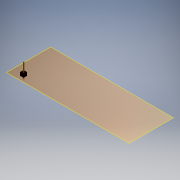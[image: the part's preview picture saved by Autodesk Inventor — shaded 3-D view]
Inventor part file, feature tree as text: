
AUTODESK INVENTOR PART (.ipt)
format: ipt  version: 2017 (Build 210142000, 142)  size: 130,048 bytes
history: native  units: mm
features: reference x5, other x3, plane x2, extrude x2, sketch x2, chamfer x1
ambient origin geometry x8: Origin, YZ Plane, XZ Plane, XY Plane, X Axis, Y Axis, Z Axis, Center Point
bodies: Solid1 (feature_tree), Solid2 (feature_tree)
feature tree (15):
  plane  "Work Plane1"
  extrude  "Extrusion1"  Depth=0.5mm
  plane  "Work Plane2"
  extrude  "Extrusion2"  Depth=2.54mm
  chamfer  "Chamfer1"  Distance=2.54mm
  sketch  "Sketch1"  dims[d0=0.5mm d1=0.5mm]
  reference  "Reference1"
  reference  "Reference2"
  sketch  "Sketch2"  dims[d2=8.0mm d3=2.0mm d4=0.0mm d5=0.0mm d6=2.54mm d7=2.54mm d8=2.0mm d9=0.0mm d10=0.2mm d11=2.0mm d12=45.0deg]
  reference  "Reference3"
  reference  "Reference4"
  reference  "Reference5"
  parser-record x1  (decoder bookkeeping rows leaked as tree rows — omitted from the tree; the rows remain in map.json)
  other  "protoswitchboard.iam"
  other  "Board:1"
note: 1 file-system path scrubbed to <path> (originals preserved in map.json)
